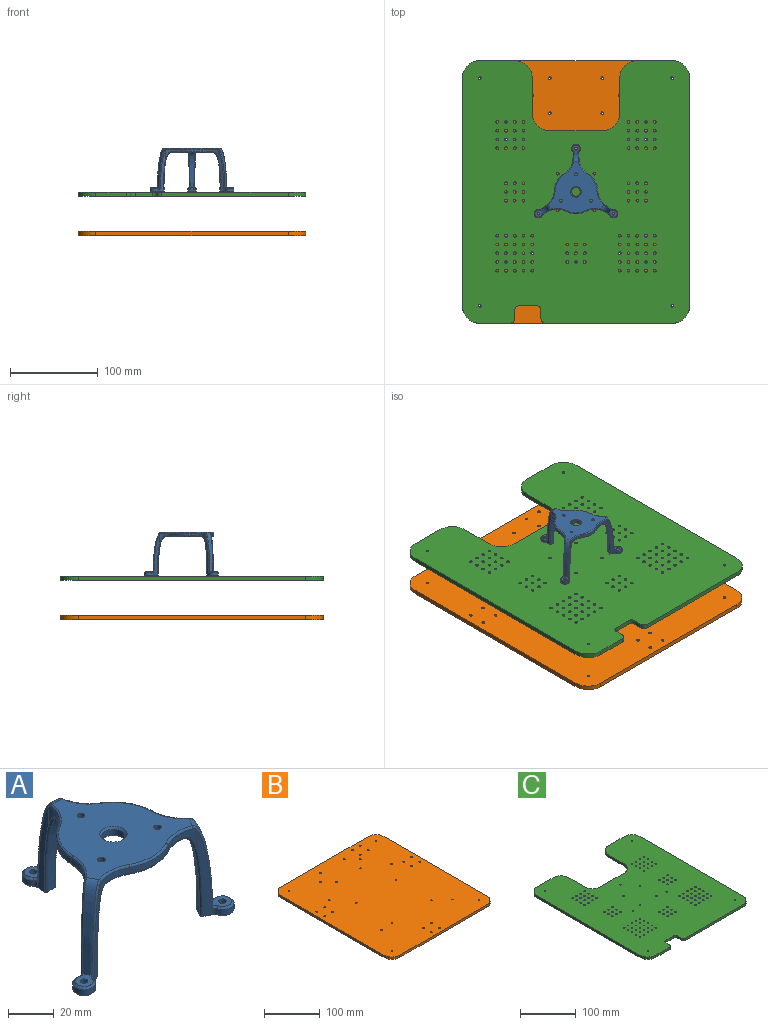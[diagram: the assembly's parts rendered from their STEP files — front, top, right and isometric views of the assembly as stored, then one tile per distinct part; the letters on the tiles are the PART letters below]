
ASSEMBLY  parts=3 mates=2
PART A: 137 faces, bbox 96.8x85.4x51.1 mm
  f0: cylinder r=25mm len=20.67mm, axis (0,0,-1), area 74.6mm2, adj f36,f41,f55,f88
  f1: plane 47.04x7.46mm, normal (1,0.09,0), area 165.7mm2, adj f36,f58,f59,f83,f94,f115,f134
  f2: plane 47.04x7.46mm, normal (-1,0.09,0), area 165.7mm2, adj f37,f49,f50,f78,f95,f116,f130
  f3: cylinder r=25mm len=20.67mm, axis (0,0,-1), area 74.6mm2, adj f37,f38,f46,f81
  f4: plane 47.04x6.14mm, normal (-0.57,0.82,0), area 165.7mm2, adj f38,f42,f43,f76,f92,f107,f129
  f5: plane 47.04x6.78mm, normal (0.42,-0.91,0), area 165.7mm2, adj f39,f67,f68,f71,f93,f108,f125
  f6: cylinder r=25mm len=23.87mm, axis (0,0,-1), area 74.6mm2, adj f39,f40,f64,f74
  f7: plane 47.04x6.78mm, normal (-0.42,-0.91,0), area 165.7mm2, adj f40,f60,f61,f69,f90,f99,f124
  f8: cylinder r=1.65mm len=5mm, axis (0,0,-1), area 51.8mm2, adj f13,f29
  f9: cylinder r=5mm len=10mm, axis (0,0,-1), area 94.2mm2, adj f135,f136
  f10: cylinder r=1.65mm len=5mm, axis (0,0,-1), area 51.8mm2, adj f13,f29
  f11: plane 47.04x6.14mm, normal (0.57,0.82,0), area 165.7mm2, adj f41,f51,f52,f85,f91,f100,f120
  f12: cylinder r=1.65mm len=5mm, axis (0,0,-1), area 51.8mm2, adj f13,f29
  f13: plane 63.22x59mm, normal (0,0,1), area 2022.7mm2, adj f8,f10,f12,f33,f34,f35,f72,f74
  f14: plane 14.07x8mm, normal (0,0,-1), area 68.1mm2, adj f17,f112,f113,f114,f115,f116,f119
  f15: plane 13.89x11.06mm, normal (0,0,-1), area 68.1mm2, adj f18,f104,f105,f106,f107,f108,f111
  f16: plane 13.89x11.06mm, normal (0,0,-1), area 68.1mm2, adj f19,f96,f97,f98,f99,f100,f103
  f17: cylinder r=1.65mm len=5mm, axis (0,0,1), area 51.8mm2, adj f14,f25
  f18: cylinder r=1.65mm len=5mm, axis (0,0,1), area 51.8mm2, adj f15,f24
  f19: cylinder r=1.65mm len=5mm, axis (0,0,1), area 51.8mm2, adj f16,f23
  f20: cylinder r=5mm len=10mm, axis (0,0,1), area 70mm2, adj f94,f95,f112,f132
  f21: cylinder r=5mm len=10mm, axis (0,0,1), area 70mm2, adj f92,f93,f104,f127
  f22: cylinder r=5mm len=10mm, axis (0,0,1), area 70mm2, adj f90,f91,f96,f122
  f23: plane 9.33x8.19mm, normal (0,0,1), area 46.9mm2, adj f19,f33,f121,f122,f123
  f24: plane 9.33x8.19mm, normal (0,0,1), area 46.9mm2, adj f18,f34,f126,f127,f128
  f25: plane 9.04x8mm, normal (0,0,1), area 46.9mm2, adj f17,f35,f131,f132,f133
  f26: cylinder r=38.5mm len=4.55mm, axis (0,0,1), area 18.2mm2, adj f32,f50,f59,f119
  f27: cylinder r=38.5mm len=4mm, axis (0,0,1), area 18.2mm2, adj f31,f42,f68,f111
  f28: cylinder r=38.5mm len=4mm, axis (0,0,1), area 18.2mm2, adj f30,f51,f60,f103
  f29: plane 55.79x54mm, normal (0,0,-1), area 1918.7mm2, adj f8,f10,f12,f30,f31,f32,f45,f46
  f30: revolved ~40x12.89mm, area 222.2mm2, adj f28,f29,f52,f53,f61,f62
  f31: revolved ~40x12.89mm, area 222.2mm2, adj f27,f29,f43,f44,f66,f67
  f32: revolved ~40x11.27mm, area 222.2mm2, adj f26,f29,f48,f49,f57,f58
  f33: revolved ~45.1x11.38mm, area 212.5mm2, adj f13,f23,f69,f70,f85,f87,f121,f123
  f34: revolved ~45.1x11.38mm, area 212.5mm2, adj f13,f24,f71,f73,f76,f77,f126,f128
  f35: revolved ~45.1x9.61mm, area 212.5mm2, adj f13,f25,f78,f80,f83,f84,f131,f133
  f36: cylinder r=20mm len=15.33mm, axis (0,0,-1), area 70.2mm2, adj f0,f1,f56,f57,f84,f86
  f37: cylinder r=20mm len=15.33mm, axis (0,0,-1), area 70.2mm2, adj f2,f3,f47,f48,f80,f82
  f38: cylinder r=20mm len=15.88mm, axis (0,0,-1), area 70.2mm2, adj f3,f4,f44,f45,f77,f79
  f39: cylinder r=20mm len=18.02mm, axis (0,0,-1), area 70.2mm2, adj f5,f6,f65,f66,f73,f75
  f40: cylinder r=20mm len=18.02mm, axis (0,0,-1), area 70.2mm2, adj f6,f7,f62,f63,f70,f72
  f41: cylinder r=20mm len=15.88mm, axis (0,0,-1), area 70.2mm2, adj f0,f11,f53,f54,f87,f89
  f42: cylinder r=1mm len=4mm, axis (0,0,1), area 6.9mm2, adj f4,f27,f43,f109
  f43: bspline ~36.44x3.88mm, area 56.7mm2, adj f4,f31,f42,f44
  f44: bspline ~10.55x6.16mm, area 18.6mm2, adj f31,f38,f43,f45
  f45: torus R=21mm, axis (0,0,-1), area 19mm2, adj f29,f38,f44,f46
  f46: torus R=24mm, axis (0,0,-1), area 38.5mm2, adj f3,f29,f45,f47
  f47: torus R=21mm, axis (0,0,-1), area 19mm2, adj f29,f37,f46,f48
  f48: bspline ~10.55x7.56mm, area 18.6mm2, adj f32,f37,f47,f49
  f49: bspline ~36.44x4.08mm, area 56.7mm2, adj f2,f32,f48,f50
  f50: cylinder r=1mm len=4mm, axis (0,0,1), area 6.9mm2, adj f2,f26,f49,f118
  f51: cylinder r=1mm len=4mm, axis (0,0,1), area 6.9mm2, adj f11,f28,f52,f102
  f52: bspline ~36.44x3.88mm, area 56.7mm2, adj f11,f30,f51,f53
  f53: bspline ~10.55x6.11mm, area 18.6mm2, adj f30,f41,f52,f54
  f54: torus R=21mm, axis (0,0,-1), area 19mm2, adj f29,f41,f53,f55
  f55: torus R=24mm, axis (0,0,-1), area 38.5mm2, adj f0,f29,f54,f56
  f56: torus R=21mm, axis (0,0,-1), area 19mm2, adj f29,f36,f55,f57
  f57: bspline ~10.55x7.62mm, area 18.6mm2, adj f32,f36,f56,f58
  f58: bspline ~37.44x4.39mm, area 56.7mm2, adj f1,f32,f57,f59
  f59: cylinder r=1mm len=4mm, axis (0,0,1), area 6.9mm2, adj f1,f26,f58,f117
  f60: cylinder r=1mm len=4mm, axis (0,0,1), area 6.9mm2, adj f7,f28,f61,f101
  f61: bspline ~37.44x3.99mm, area 56.7mm2, adj f7,f30,f60,f62
  f62: bspline ~10.55x7.14mm, area 18.6mm2, adj f30,f40,f61,f63
  f63: torus R=21mm, axis (0,0,-1), area 19mm2, adj f29,f40,f62,f64
  f64: torus R=24mm, axis (0,0,-1), area 38.5mm2, adj f6,f29,f63,f65
  f65: torus R=21mm, axis (0,0,-1), area 19mm2, adj f29,f39,f64,f66
  f66: bspline ~10.55x7.14mm, area 18.6mm2, adj f31,f39,f65,f67
  f67: bspline ~36.44x3.71mm, area 56.7mm2, adj f5,f31,f66,f68
  f68: cylinder r=1mm len=4mm, axis (0,0,1), area 6.9mm2, adj f5,f27,f67,f110
  f69: bspline ~45.66x7.74mm, area 64.8mm2, adj f7,f33,f70,f123,f124
  f70: bspline ~3.2x2.68mm, area 3.7mm2, adj f33,f40,f69,f72
  f71: bspline ~45.44x7.58mm, area 64.8mm2, adj f5,f34,f73,f125,f126
  f72: torus R=21mm, axis (0,0,1), area 27.3mm2, adj f13,f40,f70,f74
  f73: bspline ~3.2x2.68mm, area 3.7mm2, adj f34,f39,f71,f75
  f74: torus R=24mm, axis (0,0,1), area 38.5mm2, adj f6,f13,f72,f75
  f75: torus R=21mm, axis (0,0,1), area 27.3mm2, adj f13,f39,f73,f74
  f76: bspline ~45.66x6.58mm, area 64.8mm2, adj f4,f34,f77,f128,f129
  f77: bspline ~3.06x2.68mm, area 3.7mm2, adj f34,f38,f76,f79
  f78: bspline ~45.66x8.03mm, area 64.8mm2, adj f2,f35,f80,f130,f131
  f79: torus R=21mm, axis (0,0,1), area 27.3mm2, adj f13,f38,f77,f81
  f80: bspline ~3.17x2.68mm, area 3.7mm2, adj f35,f37,f78,f82
  f81: torus R=24mm, axis (0,0,1), area 38.5mm2, adj f3,f13,f79,f82
  f82: torus R=21mm, axis (0,0,1), area 27.3mm2, adj f13,f37,f80,f81
  f83: bspline ~45.44x7.86mm, area 64.8mm2, adj f1,f35,f84,f133,f134
  f84: bspline ~3.17x2.68mm, area 3.7mm2, adj f35,f36,f83,f86
  f85: bspline ~45.66x6.58mm, area 64.8mm2, adj f11,f33,f87,f120,f121
  f86: torus R=21mm, axis (0,0,1), area 27.3mm2, adj f13,f36,f84,f88
  f87: bspline ~3.06x2.68mm, area 3.7mm2, adj f33,f41,f85,f89
  f88: torus R=24mm, axis (0,0,1), area 38.5mm2, adj f0,f13,f86,f89
  f89: torus R=21mm, axis (0,0,1), area 27.3mm2, adj f13,f41,f87,f88
  f90: cylinder r=2.5mm len=3mm, axis (0,0,1), area 6.4mm2, adj f7,f22,f97,f123
  f91: cylinder r=2.5mm len=3mm, axis (0,0,1), area 6.4mm2, adj f11,f22,f98,f121
  f92: cylinder r=2.5mm len=3mm, axis (0,0,1), area 6.4mm2, adj f4,f21,f105,f128
  f93: cylinder r=2.5mm len=3mm, axis (0,0,1), area 6.4mm2, adj f5,f21,f106,f126
  f94: cylinder r=2.5mm len=3mm, axis (0,0,1), area 6.4mm2, adj f1,f20,f113,f133
  f95: cylinder r=2.5mm len=3mm, axis (0,0,1), area 6.4mm2, adj f2,f20,f114,f131
  f96: cone r=5mm half-angle=45deg, axis (0,0,1), area 29.7mm2, adj f16,f22,f97,f98
  f97: cone r=3.5mm half-angle=45deg, axis (0,0,-1), area 3.6mm2, adj f16,f90,f96,f99
  f98: cone r=3.5mm half-angle=45deg, axis (0,0,-1), area 3.6mm2, adj f16,f91,f96,f100
  f99: plane 4.59x2.86mm, normal (-0.3,-0.64,-0.71), area 6.5mm2, adj f7,f16,f97,f101
  f100: plane 4.35x3.46mm, normal (0.41,0.58,-0.71), area 6.5mm2, adj f11,f16,f98,f102
  f101: cone r=1mm half-angle=45deg, axis (0,0,1), area 1.8mm2, adj f60,f99,f103
  f102: cone r=1mm half-angle=45deg, axis (0,0,1), area 1.6mm2, adj f51,f100,f103
  f103: cone r=39.5mm half-angle=45deg, axis (0,0,-1), area 6.5mm2, adj f16,f28,f101,f102
  f104: cone r=5mm half-angle=45deg, axis (0,0,1), area 29.7mm2, adj f15,f21,f105,f106
  f105: cone r=3.5mm half-angle=45deg, axis (0,0,-1), area 3.6mm2, adj f15,f92,f104,f107
  f106: cone r=3.5mm half-angle=45deg, axis (0,0,-1), area 3.6mm2, adj f15,f93,f104,f108
  f107: plane 5.38x4.49mm, normal (-0.41,0.58,-0.71), area 6.5mm2, adj f4,f15,f105,f109
  f108: plane 4.59x2.86mm, normal (0.3,-0.64,-0.71), area 6.5mm2, adj f5,f15,f106,f110
  f109: cone r=1mm half-angle=45deg, axis (0,0,1), area 0.8mm2, adj f42,f107,f111
  f110: cone r=1mm half-angle=45deg, axis (0,0,1), area 1.8mm2, adj f68,f108,f111
  f111: cone r=39.5mm half-angle=45deg, axis (0,0,-1), area 6.5mm2, adj f15,f27,f109,f110
  f112: cone r=5mm half-angle=45deg, axis (0,0,1), area 29.7mm2, adj f14,f20,f113,f114
  f113: cone r=3.5mm half-angle=45deg, axis (0,0,-1), area 3.6mm2, adj f14,f94,f112,f115
  f114: cone r=3.5mm half-angle=45deg, axis (0,0,-1), area 3.6mm2, adj f14,f95,f112,f116
  f115: plane 4.72x1.44mm, normal (0.7,0.06,-0.71), area 6.5mm2, adj f1,f14,f113,f117
  f116: plane 5.78x2.5mm, normal (-0.7,0.06,-0.71), area 6.5mm2, adj f2,f14,f114,f118
  f117: cone r=1mm half-angle=45deg, axis (0,0,1), area 0.8mm2, adj f59,f115,f119
  f118: cone r=1mm half-angle=45deg, axis (0,0,1), area 2.2mm2, adj f50,f116,f119
  f119: cone r=39.5mm half-angle=45deg, axis (0,0,-1), area 6.5mm2, adj f14,f26,f117,f118
  f120: plane 0.56x0.55mm, normal (0.41,0.58,0.71), area 0mm2, adj f11,f85,f121
  f121: cone r=3.5mm half-angle=45deg, axis (0,0,1), area 3.3mm2, adj f23,f33,f85,f91,f120,f122
  f122: cone r=4mm half-angle=45deg, axis (0,0,-1), area 29.7mm2, adj f22,f23,f121,f123
  f123: cone r=3.5mm half-angle=45deg, axis (0,0,1), area 3.3mm2, adj f23,f33,f69,f90,f122,f124
  f124: plane 0.68x0.33mm, normal (-0.3,-0.64,0.71), area 0mm2, adj f7,f69,f123
  f125: plane 0.68x0.33mm, normal (0.3,-0.64,0.71), area 0mm2, adj f5,f71,f126
  f126: cone r=3.5mm half-angle=45deg, axis (0,0,1), area 3.3mm2, adj f24,f34,f71,f93,f125,f127
  f127: cone r=4mm half-angle=45deg, axis (0,0,-1), area 29.7mm2, adj f21,f24,f126,f128
  f128: cone r=3.5mm half-angle=45deg, axis (0,0,1), area 3.3mm2, adj f24,f34,f76,f92,f127,f129
  f129: plane 0.56x0.55mm, normal (-0.41,0.58,0.71), area 0mm2, adj f4,f76,f128
  f130: plane 0.65x0.31mm, normal (-0.7,0.06,0.71), area 0mm2, adj f2,f78,f131
  f131: cone r=3.5mm half-angle=45deg, axis (0,0,1), area 3.3mm2, adj f25,f35,f78,f95,f130,f132
  f132: cone r=4mm half-angle=45deg, axis (0,0,-1), area 29.7mm2, adj f20,f25,f131,f133
  f133: cone r=3.5mm half-angle=45deg, axis (0,0,1), area 3.3mm2, adj f25,f35,f83,f94,f132,f134
  f134: plane 0.65x0.31mm, normal (0.7,0.06,0.71), area 0mm2, adj f1,f83,f133
  f135: cone r=5mm half-angle=45deg, axis (0,0,-1), area 48.9mm2, adj f9,f29
  f136: cone r=5mm half-angle=45deg, axis (0,0,1), area 48.9mm2, adj f9,f13
PART B: 44 faces, bbox 260x300x5 mm
  f0: plane 220x5mm, normal (0,1,0), area 1100mm2, adj f38,f39,f40,f43
  f1: plane 260x5mm, normal (-1,0,0), area 1300mm2, adj f38,f39,f40,f41
  f2: plane 220x5mm, normal (0,-1,0), area 1100mm2, adj f38,f39,f41,f42
  f3: cylinder r=1.5mm len=5mm, axis (0,0,-1), area 47.1mm2, adj f38,f39
  f4: cylinder r=1.5mm len=5mm, axis (0,0,-1), area 47.1mm2, adj f38,f39
  f5: cylinder r=1.5mm len=5mm, axis (0,0,-1), area 47.1mm2, adj f38,f39
  f6: cylinder r=1.5mm len=5mm, axis (0,0,-1), area 47.1mm2, adj f38,f39
  f7: cylinder r=1.5mm len=5mm, axis (0,0,-1), area 47.1mm2, adj f38,f39
  f8: cylinder r=1.5mm len=5mm, axis (0,0,-1), area 47.1mm2, adj f38,f39
  f9: cylinder r=1.5mm len=5mm, axis (0,0,-1), area 47.1mm2, adj f38,f39
  f10: plane 260x5mm, normal (1,0,0), area 1300mm2, adj f38,f39,f42,f43
  f11: cylinder r=1.5mm len=5mm, axis (0,0,-1), area 47.1mm2, adj f38,f39
  f12: cylinder r=1.5mm len=5mm, axis (0,0,-1), area 47.1mm2, adj f38,f39
  f13: cylinder r=1.5mm len=5mm, axis (0,0,-1), area 47.1mm2, adj f38,f39
  f14: cylinder r=1.5mm len=5mm, axis (0,0,-1), area 47.1mm2, adj f38,f39
  f15: cylinder r=1.5mm len=5mm, axis (0,0,-1), area 47.1mm2, adj f38,f39
  f16: cylinder r=1.5mm len=5mm, axis (0,0,-1), area 47.1mm2, adj f38,f39
  f17: cylinder r=1.5mm len=5mm, axis (0,0,-1), area 47.1mm2, adj f38,f39
  f18: cylinder r=1.5mm len=5mm, axis (0,0,-1), area 47.1mm2, adj f38,f39
  f19: cylinder r=1.5mm len=5mm, axis (0,0,-1), area 47.1mm2, adj f38,f39
  f20: cylinder r=1.5mm len=5mm, axis (0,0,-1), area 47.1mm2, adj f38,f39
  f21: cylinder r=1.5mm len=5mm, axis (0,0,-1), area 47.1mm2, adj f38,f39
  f22: cylinder r=1.5mm len=5mm, axis (0,0,-1), area 47.1mm2, adj f38,f39
  f23: cylinder r=1.5mm len=5mm, axis (0,0,-1), area 47.1mm2, adj f38,f39
  f24: cylinder r=1.5mm len=5mm, axis (0,0,-1), area 47.1mm2, adj f38,f39
  f25: cylinder r=1.5mm len=5mm, axis (0,0,-1), area 47.1mm2, adj f38,f39
  f26: cylinder r=1.5mm len=5mm, axis (0,0,-1), area 47.1mm2, adj f38,f39
  f27: cylinder r=1.5mm len=5mm, axis (0,0,-1), area 47.1mm2, adj f38,f39
  f28: cylinder r=1.5mm len=5mm, axis (0,0,-1), area 47.1mm2, adj f38,f39
  f29: cylinder r=1.5mm len=5mm, axis (0,0,-1), area 47.1mm2, adj f38,f39
  f30: cylinder r=1.5mm len=5mm, axis (0,0,-1), area 47.1mm2, adj f38,f39
  f31: cylinder r=1.5mm len=5mm, axis (0,0,-1), area 47.1mm2, adj f38,f39
  f32: cylinder r=1.5mm len=5mm, axis (0,0,-1), area 47.1mm2, adj f38,f39
  f33: cylinder r=1.5mm len=5mm, axis (0,0,-1), area 47.1mm2, adj f38,f39
  f34: cylinder r=1.5mm len=5mm, axis (0,0,-1), area 47.1mm2, adj f38,f39
  f35: cylinder r=1.5mm len=5mm, axis (0,0,-1), area 47.1mm2, adj f38,f39
  f36: cylinder r=1.5mm len=5mm, axis (0,0,-1), area 47.1mm2, adj f38,f39
  f37: cylinder r=1.5mm len=5mm, axis (0,0,-1), area 47.1mm2, adj f38,f39
  f38: plane 300x260mm, normal (0,0,1), area 77416.3mm2, adj f0,f1,f2,f3,f4,f5,f6,f7
  f39: plane 300x260mm, normal (0,0,-1), area 77416.3mm2, adj f0,f1,f2,f3,f4,f5,f6,f7
  f40: cylinder r=20mm len=20mm, axis (0,0,1), area 157.1mm2, adj f0,f1,f38,f39
  f41: cylinder r=20mm len=20mm, axis (0,0,-1), area 157.1mm2, adj f1,f2,f38,f39
  f42: cylinder r=20mm len=20mm, axis (0,0,1), area 157.1mm2, adj f2,f10,f38,f39
  f43: cylinder r=20mm len=20mm, axis (0,0,-1), area 157.1mm2, adj f0,f10,f38,f39
PART C: 146 faces, bbox 260x300x5 mm
  f0: plane 260x5mm, normal (-1,0,0), area 1300mm2, adj f132,f133,f134,f141
  f1: plane 35x5mm, normal (0,-1,0), area 175mm2, adj f132,f133,f134,f142
  f2: plane 10x5mm, normal (1,0,0), area 50mm2, adj f132,f133,f142,f143
  f3: plane 20x5mm, normal (0,-1,0), area 100mm2, adj f132,f133,f143,f144
  f4: plane 10x5mm, normal (-1,0,0), area 50mm2, adj f132,f133,f144,f145
  f5: plane 145x5mm, normal (0,-1,0), area 725mm2, adj f132,f133,f135,f145
  f6: plane 260x5mm, normal (1,0,0), area 1300mm2, adj f132,f133,f135,f136
  f7: plane 40x5mm, normal (0,1,0), area 200mm2, adj f132,f133,f136,f137
  f8: plane 40x5mm, normal (-1,0,0), area 200mm2, adj f132,f133,f137,f138
  f9: plane 60x5mm, normal (0,1,0), area 300mm2, adj f132,f133,f138,f139
  f10: plane 40x5mm, normal (1,0,0), area 200mm2, adj f132,f133,f139,f140
  f11: cylinder r=1.5mm len=5mm, axis (0,0,-1), area 47.1mm2, adj f132,f133
  f12: cylinder r=1.5mm len=5mm, axis (0,0,-1), area 47.1mm2, adj f132,f133
  f13: cylinder r=1.5mm len=5mm, axis (0,0,-1), area 47.1mm2, adj f132,f133
  f14: cylinder r=1.5mm len=5mm, axis (0,0,-1), area 47.1mm2, adj f132,f133
  f15: cylinder r=1.5mm len=5mm, axis (0,0,-1), area 47.1mm2, adj f132,f133
  f16: cylinder r=1.5mm len=5mm, axis (0,0,-1), area 47.1mm2, adj f132,f133
  f17: cylinder r=1.5mm len=5mm, axis (0,0,-1), area 47.1mm2, adj f132,f133
  f18: cylinder r=1.5mm len=5mm, axis (0,0,-1), area 47.1mm2, adj f132,f133
  f19: cylinder r=1.5mm len=5mm, axis (0,0,-1), area 47.1mm2, adj f132,f133
  f20: cylinder r=1.5mm len=5mm, axis (0,0,-1), area 47.1mm2, adj f132,f133
  f21: cylinder r=1.5mm len=5mm, axis (0,0,-1), area 47.1mm2, adj f132,f133
  f22: cylinder r=1.5mm len=5mm, axis (0,0,-1), area 47.1mm2, adj f132,f133
  f23: cylinder r=1.5mm len=5mm, axis (0,0,-1), area 47.1mm2, adj f132,f133
  f24: cylinder r=1.5mm len=5mm, axis (0,0,-1), area 47.1mm2, adj f132,f133
  f25: cylinder r=1.5mm len=5mm, axis (0,0,-1), area 47.1mm2, adj f132,f133
  f26: cylinder r=1.5mm len=5mm, axis (0,0,-1), area 47.1mm2, adj f132,f133
  f27: cylinder r=1.5mm len=5mm, axis (0,0,-1), area 47.1mm2, adj f132,f133
  f28: cylinder r=1.5mm len=5mm, axis (0,0,-1), area 47.1mm2, adj f132,f133
  f29: cylinder r=1.5mm len=5mm, axis (0,0,-1), area 47.1mm2, adj f132,f133
  f30: cylinder r=1.5mm len=5mm, axis (0,0,-1), area 47.1mm2, adj f132,f133
  f31: cylinder r=1.5mm len=5mm, axis (0,0,-1), area 47.1mm2, adj f132,f133
  f32: cylinder r=1.5mm len=5mm, axis (0,0,-1), area 47.1mm2, adj f132,f133
  f33: cylinder r=1.5mm len=5mm, axis (0,0,-1), area 47.1mm2, adj f132,f133
  f34: cylinder r=1.5mm len=5mm, axis (0,0,-1), area 47.1mm2, adj f132,f133
  f35: cylinder r=1.5mm len=5mm, axis (0,0,-1), area 47.1mm2, adj f132,f133
  f36: cylinder r=1.5mm len=5mm, axis (0,0,-1), area 47.1mm2, adj f132,f133
  f37: cylinder r=1.5mm len=5mm, axis (0,0,-1), area 47.1mm2, adj f132,f133
  f38: cylinder r=1.5mm len=5mm, axis (0,0,-1), area 47.1mm2, adj f132,f133
  f39: cylinder r=1.5mm len=5mm, axis (0,0,-1), area 47.1mm2, adj f132,f133
  f40: cylinder r=1.5mm len=5mm, axis (0,0,-1), area 47.1mm2, adj f132,f133
  f41: cylinder r=1.5mm len=5mm, axis (0,0,-1), area 47.1mm2, adj f132,f133
  f42: cylinder r=1.5mm len=5mm, axis (0,0,-1), area 47.1mm2, adj f132,f133
  f43: cylinder r=1.5mm len=5mm, axis (0,0,-1), area 47.1mm2, adj f132,f133
  f44: cylinder r=1.5mm len=5mm, axis (0,0,-1), area 47.1mm2, adj f132,f133
  f45: cylinder r=1.5mm len=5mm, axis (0,0,-1), area 47.1mm2, adj f132,f133
  f46: cylinder r=1.5mm len=5mm, axis (0,0,-1), area 47.1mm2, adj f132,f133
  f47: cylinder r=1.5mm len=5mm, axis (0,0,-1), area 47.1mm2, adj f132,f133
  f48: cylinder r=1.5mm len=5mm, axis (0,0,-1), area 47.1mm2, adj f132,f133
  f49: cylinder r=1.5mm len=5mm, axis (0,0,-1), area 47.1mm2, adj f132,f133
  f50: cylinder r=1.5mm len=5mm, axis (0,0,-1), area 47.1mm2, adj f132,f133
  f51: cylinder r=1.5mm len=5mm, axis (0,0,-1), area 47.1mm2, adj f132,f133
  f52: cylinder r=1.5mm len=5mm, axis (0,0,-1), area 47.1mm2, adj f132,f133
  f53: cylinder r=1.5mm len=5mm, axis (0,0,-1), area 47.1mm2, adj f132,f133
  f54: cylinder r=1.5mm len=5mm, axis (0,0,-1), area 47.1mm2, adj f132,f133
  f55: cylinder r=1.5mm len=5mm, axis (0,0,-1), area 47.1mm2, adj f132,f133
  f56: cylinder r=1.5mm len=5mm, axis (0,0,-1), area 47.1mm2, adj f132,f133
  f57: cylinder r=1.5mm len=5mm, axis (0,0,-1), area 47.1mm2, adj f132,f133
  f58: cylinder r=1.5mm len=5mm, axis (0,0,-1), area 47.1mm2, adj f132,f133
  f59: cylinder r=1.5mm len=5mm, axis (0,0,-1), area 47.1mm2, adj f132,f133
  f60: cylinder r=1.5mm len=5mm, axis (0,0,-1), area 47.1mm2, adj f132,f133
  f61: cylinder r=1.5mm len=5mm, axis (0,0,-1), area 47.1mm2, adj f132,f133
  f62: cylinder r=1.5mm len=5mm, axis (0,0,-1), area 47.1mm2, adj f132,f133
  f63: cylinder r=1.5mm len=5mm, axis (0,0,-1), area 47.1mm2, adj f132,f133
  f64: cylinder r=1.5mm len=5mm, axis (0,0,-1), area 47.1mm2, adj f132,f133
  f65: cylinder r=1.5mm len=5mm, axis (0,0,-1), area 47.1mm2, adj f132,f133
  f66: cylinder r=1.5mm len=5mm, axis (0,0,-1), area 47.1mm2, adj f132,f133
  f67: cylinder r=1.5mm len=5mm, axis (0,0,-1), area 47.1mm2, adj f132,f133
  f68: cylinder r=1.5mm len=5mm, axis (0,0,-1), area 47.1mm2, adj f132,f133
  f69: cylinder r=1.5mm len=5mm, axis (0,0,-1), area 47.1mm2, adj f132,f133
  f70: cylinder r=1.5mm len=5mm, axis (0,0,-1), area 47.1mm2, adj f132,f133
  f71: cylinder r=1.5mm len=5mm, axis (0,0,-1), area 47.1mm2, adj f132,f133
  f72: cylinder r=1.5mm len=5mm, axis (0,0,-1), area 47.1mm2, adj f132,f133
  f73: cylinder r=1.5mm len=5mm, axis (0,0,-1), area 47.1mm2, adj f132,f133
  f74: cylinder r=1.5mm len=5mm, axis (0,0,-1), area 47.1mm2, adj f132,f133
  f75: cylinder r=1.5mm len=5mm, axis (0,0,-1), area 47.1mm2, adj f132,f133
  f76: cylinder r=1.5mm len=5mm, axis (0,0,-1), area 47.1mm2, adj f132,f133
  f77: cylinder r=1.5mm len=5mm, axis (0,0,-1), area 47.1mm2, adj f132,f133
  f78: cylinder r=1.5mm len=5mm, axis (0,0,-1), area 47.1mm2, adj f132,f133
  f79: cylinder r=1.5mm len=5mm, axis (0,0,-1), area 47.1mm2, adj f132,f133
  f80: cylinder r=1.5mm len=5mm, axis (0,0,-1), area 47.1mm2, adj f132,f133
  f81: cylinder r=1.5mm len=5mm, axis (0,0,-1), area 47.1mm2, adj f132,f133
  f82: cylinder r=1.5mm len=5mm, axis (0,0,-1), area 47.1mm2, adj f132,f133
  f83: cylinder r=1.5mm len=5mm, axis (0,0,-1), area 47.1mm2, adj f132,f133
  f84: cylinder r=1.5mm len=5mm, axis (0,0,-1), area 47.1mm2, adj f132,f133
  f85: cylinder r=1.5mm len=5mm, axis (0,0,-1), area 47.1mm2, adj f132,f133
  f86: cylinder r=1.5mm len=5mm, axis (0,0,-1), area 47.1mm2, adj f132,f133
  f87: plane 40x5mm, normal (0,1,0), area 200mm2, adj f132,f133,f140,f141
  f88: cylinder r=1.5mm len=5mm, axis (0,0,-1), area 47.1mm2, adj f132,f133
  f89: cylinder r=1.5mm len=5mm, axis (0,0,-1), area 47.1mm2, adj f132,f133
  f90: cylinder r=1.5mm len=5mm, axis (0,0,-1), area 47.1mm2, adj f132,f133
  f91: cylinder r=1.5mm len=5mm, axis (0,0,-1), area 47.1mm2, adj f132,f133
  f92: cylinder r=1.5mm len=5mm, axis (0,0,-1), area 47.1mm2, adj f132,f133
  f93: cylinder r=1.5mm len=5mm, axis (0,0,-1), area 47.1mm2, adj f132,f133
  f94: cylinder r=1.5mm len=5mm, axis (0,0,-1), area 47.1mm2, adj f132,f133
  f95: cylinder r=1.5mm len=5mm, axis (0,0,-1), area 47.1mm2, adj f132,f133
  f96: cylinder r=1.5mm len=5mm, axis (0,0,-1), area 47.1mm2, adj f132,f133
  f97: cylinder r=1.5mm len=5mm, axis (0,0,-1), area 47.1mm2, adj f132,f133
  f98: cylinder r=1.5mm len=5mm, axis (0,0,-1), area 47.1mm2, adj f132,f133
  f99: cylinder r=1.5mm len=5mm, axis (0,0,-1), area 47.1mm2, adj f132,f133
  f100: cylinder r=1.5mm len=5mm, axis (0,0,-1), area 47.1mm2, adj f132,f133
  f101: cylinder r=1.5mm len=5mm, axis (0,0,-1), area 47.1mm2, adj f132,f133
  f102: cylinder r=1.5mm len=5mm, axis (0,0,-1), area 47.1mm2, adj f132,f133
  f103: cylinder r=1.5mm len=5mm, axis (0,0,-1), area 47.1mm2, adj f132,f133
  f104: cylinder r=1.5mm len=5mm, axis (0,0,-1), area 47.1mm2, adj f132,f133
  f105: cylinder r=1.5mm len=5mm, axis (0,0,-1), area 47.1mm2, adj f132,f133
  f106: cylinder r=1.5mm len=5mm, axis (0,0,-1), area 47.1mm2, adj f132,f133
  f107: cylinder r=1.5mm len=5mm, axis (0,0,-1), area 47.1mm2, adj f132,f133
  f108: cylinder r=1.5mm len=5mm, axis (0,0,-1), area 47.1mm2, adj f132,f133
  f109: cylinder r=1.5mm len=5mm, axis (0,0,-1), area 47.1mm2, adj f132,f133
  f110: cylinder r=1.5mm len=5mm, axis (0,0,-1), area 47.1mm2, adj f132,f133
  f111: cylinder r=1.5mm len=5mm, axis (0,0,-1), area 47.1mm2, adj f132,f133
  f112: cylinder r=1.5mm len=5mm, axis (0,0,-1), area 47.1mm2, adj f132,f133
  f113: cylinder r=1.5mm len=5mm, axis (0,0,-1), area 47.1mm2, adj f132,f133
  f114: cylinder r=1.5mm len=5mm, axis (0,0,-1), area 47.1mm2, adj f132,f133
  f115: cylinder r=1.5mm len=5mm, axis (0,0,-1), area 47.1mm2, adj f132,f133
  f116: cylinder r=1.5mm len=5mm, axis (0,0,-1), area 47.1mm2, adj f132,f133
  f117: cylinder r=1.5mm len=5mm, axis (0,0,-1), area 47.1mm2, adj f132,f133
  f118: cylinder r=1.5mm len=5mm, axis (0,0,-1), area 47.1mm2, adj f132,f133
  f119: cylinder r=1.5mm len=5mm, axis (0,0,-1), area 47.1mm2, adj f132,f133
  f120: cylinder r=1.5mm len=5mm, axis (0,0,-1), area 47.1mm2, adj f132,f133
  f121: cylinder r=1.5mm len=5mm, axis (0,0,-1), area 47.1mm2, adj f132,f133
  f122: cylinder r=1.5mm len=5mm, axis (0,0,-1), area 47.1mm2, adj f132,f133
  f123: cylinder r=1.5mm len=5mm, axis (0,0,-1), area 47.1mm2, adj f132,f133
  f124: cylinder r=1.5mm len=5mm, axis (0,0,-1), area 47.1mm2, adj f132,f133
  f125: cylinder r=1.5mm len=5mm, axis (0,0,-1), area 47.1mm2, adj f132,f133
  f126: cylinder r=1.5mm len=5mm, axis (0,0,-1), area 47.1mm2, adj f132,f133
  f127: cylinder r=1.5mm len=5mm, axis (0,0,-1), area 47.1mm2, adj f132,f133
  f128: cylinder r=1.5mm len=5mm, axis (0,0,-1), area 47.1mm2, adj f132,f133
  f129: cylinder r=1.5mm len=5mm, axis (0,0,-1), area 47.1mm2, adj f132,f133
  f130: cylinder r=1.5mm len=5mm, axis (0,0,-1), area 47.1mm2, adj f132,f133
  f131: cylinder r=1.5mm len=5mm, axis (0,0,-1), area 47.1mm2, adj f132,f133
  f132: plane 300x260mm, normal (0,0,1), area 68208.4mm2, adj f0,f1,f2,f3,f4,f5,f6,f7
  f133: plane 300x260mm, normal (0,0,-1), area 68208.4mm2, adj f0,f1,f2,f3,f4,f5,f6,f7
  f134: cylinder r=20mm len=20mm, axis (0,0,-1), area 157.1mm2, adj f0,f1,f132,f133
  f135: cylinder r=20mm len=20mm, axis (0,0,1), area 157.1mm2, adj f5,f6,f132,f133
  f136: cylinder r=20mm len=20mm, axis (0,0,-1), area 157.1mm2, adj f6,f7,f132,f133
  f137: cylinder r=20mm len=20mm, axis (0,0,1), area 157.1mm2, adj f7,f8,f132,f133
  f138: cylinder r=20mm len=20mm, axis (0,0,-1), area 157.1mm2, adj f8,f9,f132,f133
  f139: cylinder r=20mm len=20mm, axis (0,0,1), area 157.1mm2, adj f9,f10,f132,f133
  f140: cylinder r=20mm len=20mm, axis (0,0,-1), area 157.1mm2, adj f10,f87,f132,f133
  f141: cylinder r=20mm len=20mm, axis (0,0,1), area 157.1mm2, adj f0,f87,f132,f133
  f142: cylinder r=5mm len=5mm, axis (0,0,-1), area 39.3mm2, adj f1,f2,f132,f133
  f143: cylinder r=5mm len=5mm, axis (0,0,1), area 39.3mm2, adj f2,f3,f132,f133
  f144: cylinder r=5mm len=5mm, axis (0,0,-1), area 39.3mm2, adj f3,f4,f132,f133
  f145: cylinder r=5mm len=5mm, axis (0,0,1), area 39.3mm2, adj f4,f5,f132,f133
PLACE A t=(3.34,-5.23,27.86)mm
PLACE B t=(3.34,14.77,-67.14)mm
PLACE C t=(3.34,-5.23,-22.14)mm
MATE fastened A.f18 <-> C.f77  axis (0,0,-1) through (-39.53,-29.98,-17.14)mm
MATE fastened B.f16 <-> C.f86  axis (0,0,1) through (-106.66,-135.23,-62.14)mm
